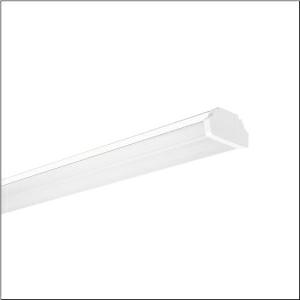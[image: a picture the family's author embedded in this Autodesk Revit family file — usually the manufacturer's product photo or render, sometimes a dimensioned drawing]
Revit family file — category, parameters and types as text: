
# Revit family: dus_r__31_mo_53bd812m1v4085_035f
name_source: partatom
category: Lighting Fixtures
units: mm (PartAtom-declared; Revit-internal decimal feet)

## family parameters
Cut with Voids When Loaded = No
Host = Face
Light Source = No
Part Type = Normal
Room Calculation Point = No
Round Connector Dimension = Use Diameter
Shared = No

## types (1)
- --- (1 x LED, 8950 lm, 59.6 W, 4000K)
    Apparent Load = 60 VA
    CIE Flux Codes = 47 80 95 92 100
    Color Rendering = 80
    Color Temperature = 4000K
    Default Elevation = 1800 mm
    Description = DUS® 31 MO, luminaire insert, of sheet steel, coil coated, white, length: 1.535mm, width: 81mm, height: 90mm, 5x system unit, system units: 307mm, LED rated luminous flux: 8.950lm, light colour: 840, control gear: ON/OFF Multilumen, control gear: ECG Multilumen, with plug, 3-pole, with phase selection, mains connection: 220..240V, AC, 50/60Hz, rated input power: 60W, through-wiring accessed according to module size, primary optical cover: cover, of PMMA, light emission: direct distribution, primary light characteristic: symmetric, protection rating (complete): IP20, protection rating (LED compartment): IP50, insulation class (complete): insulation class I (protective earthing), certification: CE, ENEC, VDE, UKCA, impact resistance: IK03, permissible ambient temperature for indoor applications: -35..+30°C, corresponds to IFS (International Featured Standards) requirements for safety and quality in the food industry, reducing of maximum allowable ambient temperature of 5°C with ceiling mounting, packaging unit: 1 piece
    Height = 95 mm
    Lamp = 1 x LED
    Lamp Light Flux = 8950 lm
    Lamp Power = 59.6 W
    Lamp count = 1
    Length = 1535 mm
    Luminous efficacy = 150 lm/W
    Manufacturer = Siteco
    ModVariant = No
    Model = 53BD812M1V4085
    Mounting Place = Ceiling
    Mounting Type = Pendant
    Number of Poles = 1
    OnlyDefault = Yes
    Power Factor = 1
    Product Name = DUS® 31 MO
    Product group = luminaire insert
    ProductGroupID = 901
    Protection Class = Protection class I
    Protection Degree = IP 20
    RLX_Detail_Level = 1
    RLX_Emergency_Light_Flux = 0 lm
    RLX_Emergency_Type = 0
    RLX_Emergency_Type_DB = No
    RlxData = <blob elided: 39777 chars, md5=c56ff6f8>
    Socket = socket
    Standby Power = 0 W
    System Light Flux = 8950 lm
    System Power = 60 W
    Type Comments = factory setting: luminous flux: 100 % | (A | C | E) | 129 mA
    Type Image = l_1003451.jpg
    URL = http://relux.com
    VarID = @adj_140345
    Voltage = 0 V
    Weight = 0.00 kg
    Width = 81 mm

## geometry (parser evidence)
native form markers: Blend x4, Sweep x14
no freeform markers — native parametric forms only
